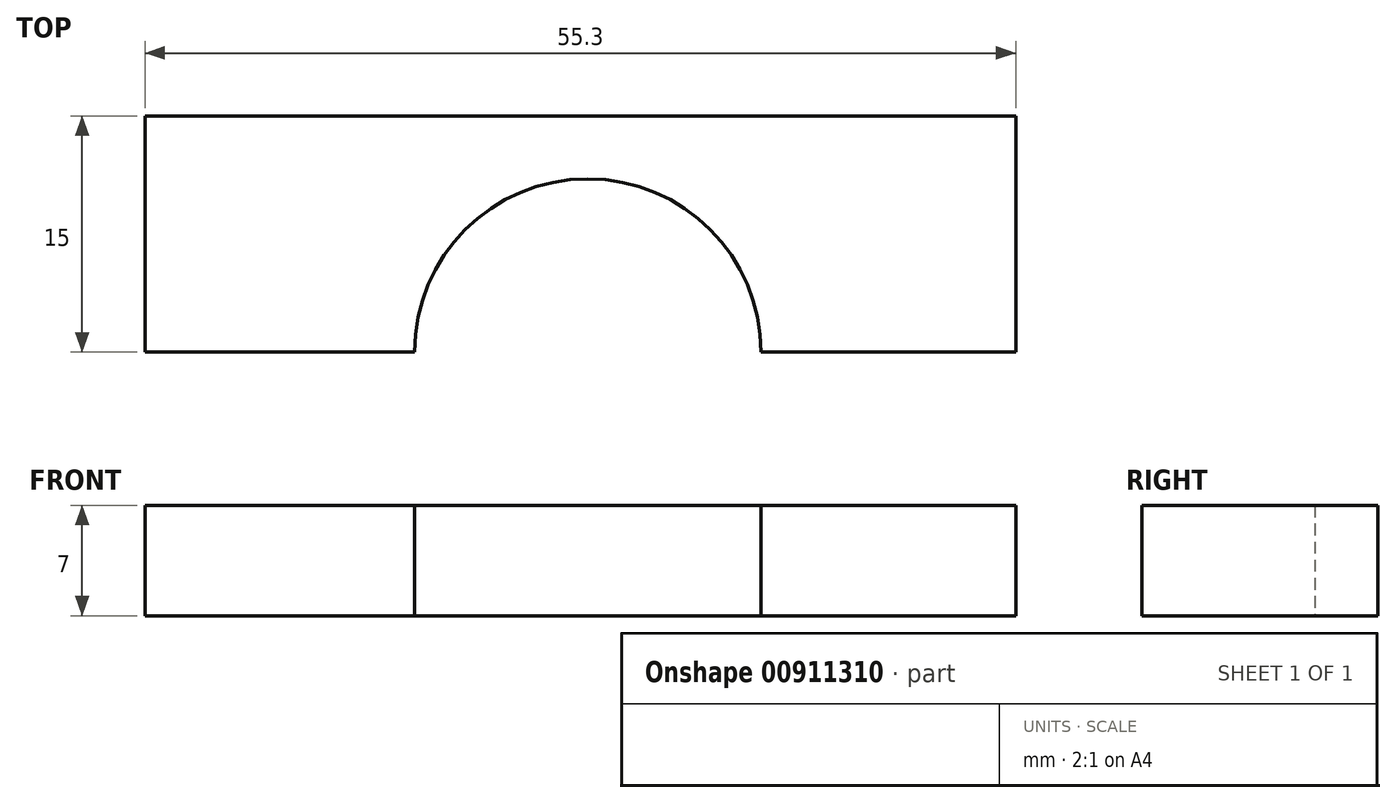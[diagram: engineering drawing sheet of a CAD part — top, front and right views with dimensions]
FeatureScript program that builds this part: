
annotation { "Feature Type Name" : "Feature", "Feature Type Description" : "" }
export const myFeature = defineFeature(function(context is Context, id is Id, definition is map)
    precondition{}
    {
        {
            var Q0;
            Q0=qCreatedBy(makeId("Top.planeOp"),FACE);
            var sketch = newSketch(context, id + "F0", { "sketchPlane" : qUnion([Q0])});
            skCircle(sketch, "E0", {"center": v(0, 0) * mm, "radius": 11 * mm});
            skLineSegment(sketch, "E1", {"start": v(0, 0) * mm, "end": v(0, 15) * mm});
            skLineSegment(sketch, "E2", {"start": v(0, 15) * mm, "end": v(27.2, 15) * mm});
            skLineSegment(sketch, "E3", {"start": v(27.2, 15) * mm, "end": v(27.2, 0) * mm});
            skLineSegment(sketch, "E4", {"start": v(27.2, 0) * mm, "end": v(0, 0) * mm});
            skLineSegment(sketch, "E5", {"start": v(0, 0) * mm, "end": v(-28.11, 0) * mm});
            skLineSegment(sketch, "E6", {"start": v(-28.11, 0) * mm, "end": v(-28.11, 15) * mm});
            skLineSegment(sketch, "E7", {"start": v(-28.11, 15) * mm, "end": v(0, 15) * mm});
            skSolve(sketch);
        }
        {
            var Q0;
            {var subQ0=sQuery(id+"F0.wireOp",EDGE,"E6");Q0=makeQuery(id+"F0.imprint","IMPRINT",FACE,{"disambiguationData":[TD([[makeQuery(id+"F0.imprint","IMPRINT",EDGE,{"derivedFrom":subQ0}),-1.0]])]});}
            var Q1;
            {var subQ1=sQuery(id+"F0.wireOp",EDGE,"E2");Q1=makeQuery(id+"F0.imprint","IMPRINT",FACE,{"disambiguationData":[TD([[makeQuery(id+"F0.imprint","IMPRINT",EDGE,{"derivedFrom":subQ1}),-1.0]])]});}
            extrude(context, id + "F1", {"entities" : qUnion([Q0, Q1]), "depth" : 7 * mm, "offsetDistance" : 25 * mm});
        }
    });
